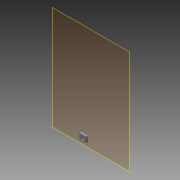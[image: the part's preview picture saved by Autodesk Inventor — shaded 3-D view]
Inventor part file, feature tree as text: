
AUTODESK INVENTOR PART (.ipt)
format: ipt  version: 2013 (Build 170138000, 138)  size: 91,648 bytes
history: native  units: in
note: dims shown in document units (in); Inventor stores cm internally (conversion verified against a paired STEP export)
features: reference x3, plane x1, extrude x1, fillet x1, sketch x1
ambient origin geometry x8: Origin, YZ Plane, XZ Plane, XY Plane, X Axis, Y Axis, Z Axis, Center Point
bodies: Solid1 (feature_tree)
feature tree (7):
  plane  "Work Plane1"
  extrude  "Extrusion1"  Depth=0.9843in
  fillet  "Fillet1"  Radius=0.0394in
  sketch  "Sketch1"  dims[d0=0.7874in d2=0.9843in d3=0.0394in d4=0.255in d5=0.0in d6=0.1969in]
  reference  "Reference1"
  reference  "Reference2"
  reference  "Reference3"
